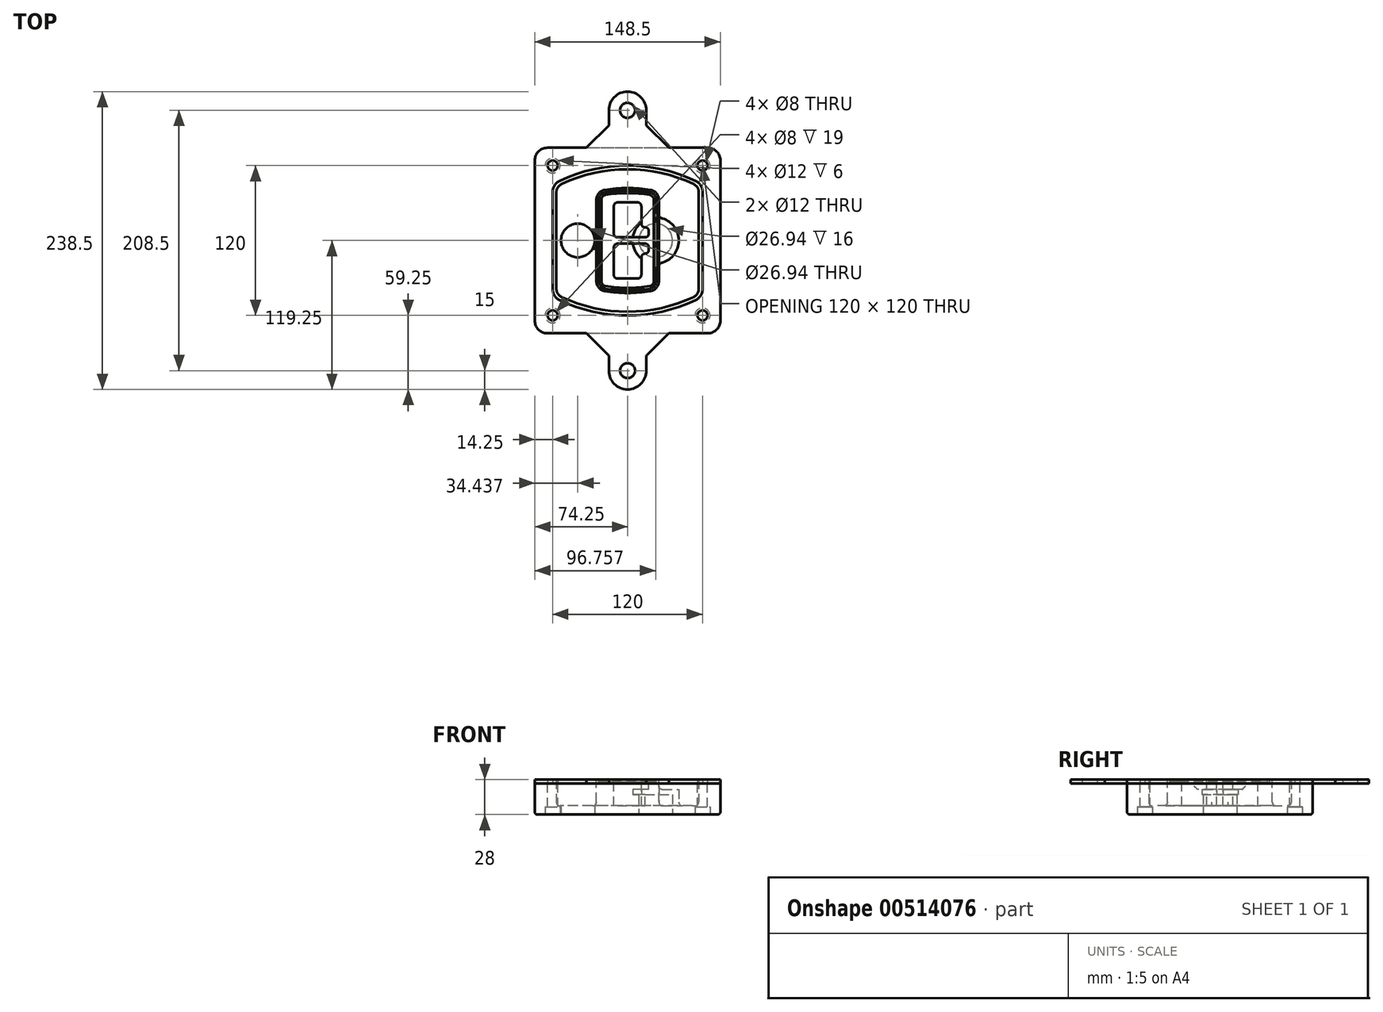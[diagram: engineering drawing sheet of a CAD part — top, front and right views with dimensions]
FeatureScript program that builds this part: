
annotation { "Feature Type Name" : "Feature", "Feature Type Description" : "" }
export const myFeature = defineFeature(function(context is Context, id is Id, definition is map)
    precondition{}
    {
        {
            var Q0;
            Q0=qCreatedBy(makeId("Top.planeOp"),FACE);
            var sketch = newSketch(context, id + "F0", { "sketchPlane" : qUnion([Q0])});
            skPoint(sketch, "E0.rect.middle", {"position": v(0, 0) * mm});
            skLineSegment(sketch, "E1.bottom", {"start": v(-64.25, -74.25) * mm, "end": v(64.25, -74.25) * mm});
            skLineSegment(sketch, "E1.top", {"start": v(-64.25, 74.25) * mm, "end": v(64.25, 74.25) * mm});
            skLineSegment(sketch, "E1.left", {"start": v(-74.25, -64.25) * mm, "end": v(-74.25, 64.25) * mm});
            skLineSegment(sketch, "E1.right", {"start": v(74.25, -64.25) * mm, "end": v(74.25, 64.25) * mm});
            skLineSegment(sketch, "E2", {"start": v(-74.25, 74.25) * mm, "end": v(74.25, -74.25) * mm, "construction": true});
            skLineSegment(sketch, "E3", {"start": v(74.25, 74.25) * mm, "end": v(-74.25, -74.25) * mm, "construction": true});
            skCircle(sketch, "E4", {"center": v(-60, 60) * mm, "radius": 4 * mm});
            skCircle(sketch, "E5", {"center": v(60, 60) * mm, "radius": 4 * mm});
            skCircle(sketch, "E6", {"center": v(60, -60) * mm, "radius": 4 * mm});
            skCircle(sketch, "E7", {"center": v(-60, -60) * mm, "radius": 4 * mm});
            skLineSegment(sketch, "E8", {"start": v(-60, 60) * mm, "end": v(60, 60) * mm, "construction": true});
            skLineSegment(sketch, "E9", {"start": v(60, 60) * mm, "end": v(60, -60) * mm, "construction": true});
            skLineSegment(sketch, "E10", {"start": v(60, -60) * mm, "end": v(-60, -60) * mm, "construction": true});
            skLineSegment(sketch, "E11", {"start": v(-60, -60) * mm, "end": v(-60, 60) * mm, "construction": true});
            skLineSegment(sketch, "E12", {"start": v(-60, 38.83) * mm, "end": v(-60, -38.83) * mm});
            skLineSegment(sketch, "E13", {"start": v(60, 38.83) * mm, "end": v(60, -38.83) * mm});
            skArc(sketch, "E14", {"start": v(54.26, 47.88) * mm, "mid": v(0, 60) * mm, "end": v(-54.26, 47.88) * mm});
            skArc(sketch, "E15", {"start": v(-54.26, -47.88) * mm, "mid": v(0, -60) * mm, "end": v(54.26, -47.88) * mm});
            skLineSegment(sketch, "E16", {"start": v(-60, 0) * mm, "end": v(60, 0) * mm, "construction": true});
            skPoint(sketch, "E17.visualSharp", {"position": v(-60, -45) * mm});
            skArc(sketch, "E17.filletArc", {"start": v(-60, -38.83) * mm, "mid": v(-58.44, -44.2) * mm, "end": v(-54.26, -47.88) * mm});
            skPoint(sketch, "E18.visualSharp", {"position": v(-60, 45) * mm});
            skArc(sketch, "E18.filletArc", {"start": v(-54.26, 47.88) * mm, "mid": v(-58.44, 44.2) * mm, "end": v(-60, 38.83) * mm});
            skPoint(sketch, "E19.visualSharp", {"position": v(60, 45) * mm});
            skArc(sketch, "E19.filletArc", {"start": v(60, 38.83) * mm, "mid": v(58.44, 44.2) * mm, "end": v(54.26, 47.88) * mm});
            skPoint(sketch, "E20.visualSharp", {"position": v(60, -45) * mm});
            skArc(sketch, "E20.filletArc", {"start": v(54.26, -47.88) * mm, "mid": v(58.44, -44.2) * mm, "end": v(60, -38.83) * mm});
            skPoint(sketch, "E21.visualSharp", {"position": v(-74.25, 74.25) * mm});
            skArc(sketch, "E21.filletArc", {"start": v(-64.25, 74.25) * mm, "mid": v(-71.32, 71.32) * mm, "end": v(-74.25, 64.25) * mm});
            skPoint(sketch, "E22.visualSharp", {"position": v(74.25, 74.25) * mm});
            skArc(sketch, "E22.filletArc", {"start": v(74.25, 64.25) * mm, "mid": v(71.32, 71.32) * mm, "end": v(64.25, 74.25) * mm});
            skPoint(sketch, "E23.visualSharp", {"position": v(74.25, -74.25) * mm});
            skArc(sketch, "E23.filletArc", {"start": v(64.25, -74.25) * mm, "mid": v(71.32, -71.32) * mm, "end": v(74.25, -64.25) * mm});
            skPoint(sketch, "E24.visualSharp", {"position": v(-74.25, -74.25) * mm});
            skArc(sketch, "E24.filletArc", {"start": v(-74.25, -64.25) * mm, "mid": v(-71.32, -71.32) * mm, "end": v(-64.25, -74.25) * mm});
            skArc(sketch, "E25.0", {"start": v(57, 38.83) * mm, "mid": v(55.9, 42.58) * mm, "end": v(52.98, 45.17) * mm});
            skLineSegment(sketch, "E25.1", {"start": v(57, 38.83) * mm, "end": v(57, -38.83) * mm});
            skArc(sketch, "E25.2", {"start": v(52.98, -45.17) * mm, "mid": v(55.9, -42.58) * mm, "end": v(57, -38.83) * mm});
            skArc(sketch, "E25.3", {"start": v(-52.98, -45.17) * mm, "mid": v(0, -57) * mm, "end": v(52.98, -45.17) * mm});
            skArc(sketch, "E25.4", {"start": v(-57, -38.83) * mm, "mid": v(-55.9, -42.58) * mm, "end": v(-52.98, -45.17) * mm});
            skArc(sketch, "E25.5", {"start": v(52.98, 45.17) * mm, "mid": v(0, 57) * mm, "end": v(-52.98, 45.17) * mm});
            skLineSegment(sketch, "E25.6", {"start": v(-57, 38.83) * mm, "end": v(-57, -38.83) * mm});
            skArc(sketch, "E25.7", {"start": v(-52.98, 45.17) * mm, "mid": v(-55.9, 42.58) * mm, "end": v(-57, 38.83) * mm});
            skArc(sketch, "E26.0", {"start": v(-55.96, 51.5) * mm, "mid": v(-61.82, 46.33) * mm, "end": v(-64, 38.83) * mm});
            skArc(sketch, "E26.1", {"start": v(55.96, 51.5) * mm, "mid": v(0, 64) * mm, "end": v(-55.96, 51.5) * mm});
            skArc(sketch, "E26.2", {"start": v(64, 38.83) * mm, "mid": v(61.82, 46.33) * mm, "end": v(55.96, 51.5) * mm});
            skLineSegment(sketch, "E26.3", {"start": v(64, 38.83) * mm, "end": v(64, -38.83) * mm});
            skArc(sketch, "E26.4", {"start": v(55.96, -51.5) * mm, "mid": v(61.82, -46.33) * mm, "end": v(64, -38.83) * mm});
            skLineSegment(sketch, "E26.5", {"start": v(-64, 38.83) * mm, "end": v(-64, -38.83) * mm});
            skArc(sketch, "E26.6", {"start": v(-55.96, -51.5) * mm, "mid": v(0, -64) * mm, "end": v(55.96, -51.5) * mm});
            skArc(sketch, "E26.7", {"start": v(-64, -38.83) * mm, "mid": v(-61.82, -46.33) * mm, "end": v(-55.96, -51.5) * mm});
            skSolve(sketch);
        }
        {
            var Q0;
            Q0=makeQuery(id+"F0.imprint","IMPRINT",FACE,{"disambiguationData":[TD([[makeQuery(id+"F0.imprint","IMPRINT",EDGE,{"derivedFrom":sQuery(id+"F0.wireOp",EDGE,"E1.bottom")}),1.0]])]});
            var Q1;
            Q1=makeQuery(id+"F0.imprint","IMPRINT",FACE,{"disambiguationData":[TD([[makeQuery(id+"F0.imprint","IMPRINT",EDGE,{"derivedFrom":sQuery(id+"F0.wireOp",EDGE,"E12")}),1.0]])]});
            var Q2;
            Q2=makeQuery(id+"F0.imprint","IMPRINT",FACE,{"disambiguationData":[TD([[makeQuery(id+"F0.imprint","IMPRINT",EDGE,{"derivedFrom":sQuery(id+"F0.wireOp",EDGE,"E25.0")}),1.0]])]});
            var Q3;
            Q3=makeQuery(id+"F0.imprint","IMPRINT",FACE,{"disambiguationData":[TD([[makeQuery(id+"F0.imprint","IMPRINT",EDGE,{"derivedFrom":sQuery(id+"F0.wireOp",EDGE,"E12")}),-1.0]])]});
            extrude(context, id + "F1", {"entities" : qUnion([Q0, Q1, Q2, Q3]), "oppositeDirection" : true, "depth" : 25 * mm});
        }
        {
            var Q0;
            Q0=makeQuery(id+"F0.imprint","IMPRINT",FACE,{"disambiguationData":[TD([[makeQuery(id+"F0.imprint","IMPRINT",EDGE,{"derivedFrom":sQuery(id+"F0.wireOp",EDGE,"E12")}),1.0]])]});
            extrude(context, id + "F2", {"entities" : qUnion([Q0]), "operationType" : NewBodyOperationType.ADD, "depth" : 3 * mm});
        }
        {
            var Q0;
            Q0=makeQuery(id+"F0.imprint","IMPRINT",FACE,{"disambiguationData":[TD([[makeQuery(id+"F0.imprint","IMPRINT",EDGE,{"derivedFrom":sQuery(id+"F0.wireOp",EDGE,"E25.0")}),1.0]])]});
            extrude(context, id + "F3", {"entities" : qUnion([Q0]), "operationType" : NewBodyOperationType.REMOVE, "oppositeDirection" : true, "depth" : 18 * mm});
        }
        {
            var Q0;
            Q0=makeQuery(id+"F2.opExtrude","CAP_FACE",FACE,{"disambiguationData":[OSD([sQuery(id+"F0.wireOp",EDGE,"E12"),sQuery(id+"F0.wireOp",EDGE,"E13"),sQuery(id+"F0.wireOp",EDGE,"E14"),sQuery(id+"F0.wireOp",EDGE,"E15"),sQuery(id+"F0.wireOp",EDGE,"E17.filletArc"),sQuery(id+"F0.wireOp",EDGE,"E18.filletArc"),sQuery(id+"F0.wireOp",EDGE,"E19.filletArc"),sQuery(id+"F0.wireOp",EDGE,"E20.filletArc"),sQuery(id+"F0.wireOp",EDGE,"E25.0"),sQuery(id+"F0.wireOp",EDGE,"E25.1"),sQuery(id+"F0.wireOp",EDGE,"E25.2"),sQuery(id+"F0.wireOp",EDGE,"E25.3"),sQuery(id+"F0.wireOp",EDGE,"E25.4"),sQuery(id+"F0.wireOp",EDGE,"E25.5"),sQuery(id+"F0.wireOp",EDGE,"E25.6"),sQuery(id+"F0.wireOp",EDGE,"E25.7")])],"isStart":false});
            var sketch = newSketch(context, id + "F4", { "sketchPlane" : qUnion([Q0])});
            skArc(sketch, "E27.0", {"start": v(-18.34, -40.45) * mm, "mid": v(0, -42) * mm, "end": v(18.34, -40.45) * mm});
            skArc(sketch, "E28.0", {"start": v(18.34, 40.45) * mm, "mid": v(0, 42) * mm, "end": v(-18.34, 40.45) * mm});
            skLineSegment(sketch, "E29", {"start": v(-25, 32.57) * mm, "end": v(-25, -32.57) * mm});
            skLineSegment(sketch, "E30", {"start": v(25, 32.57) * mm, "end": v(25, -32.57) * mm});
            skLineSegment(sketch, "E31", {"start": v(-25, 39.1) * mm, "end": v(25, 39.1) * mm, "construction": true});
            skLineSegment(sketch, "E32", {"start": v(-25, -39.1) * mm, "end": v(25, -39.1) * mm, "construction": true});
            skPoint(sketch, "E33.visualSharp", {"position": v(-25, 39.1) * mm});
            skArc(sketch, "E33.filletArc", {"start": v(-18.34, 40.45) * mm, "mid": v(-23.11, 37.73) * mm, "end": v(-25, 32.57) * mm});
            skPoint(sketch, "E34.visualSharp", {"position": v(25, 39.1) * mm});
            skArc(sketch, "E34.filletArc", {"start": v(25, 32.57) * mm, "mid": v(23.11, 37.73) * mm, "end": v(18.34, 40.45) * mm});
            skPoint(sketch, "E35.visualSharp", {"position": v(25, -39.1) * mm});
            skArc(sketch, "E35.filletArc", {"start": v(18.34, -40.45) * mm, "mid": v(23.11, -37.73) * mm, "end": v(25, -32.57) * mm});
            skPoint(sketch, "E36.visualSharp", {"position": v(-25, -39.1) * mm});
            skArc(sketch, "E36.filletArc", {"start": v(-25, -32.57) * mm, "mid": v(-23.11, -37.73) * mm, "end": v(-18.34, -40.45) * mm});
            skArc(sketch, "E37.0", {"start": v(52.98, 45.17) * mm, "mid": v(0, 57) * mm, "end": v(-52.98, 45.17) * mm});
            skArc(sketch, "E37.1", {"start": v(-52.98, 45.17) * mm, "mid": v(-55.9, 42.58) * mm, "end": v(-57, 38.83) * mm});
            skLineSegment(sketch, "E37.2", {"start": v(-57, 38.83) * mm, "end": v(-57, -38.83) * mm});
            skArc(sketch, "E37.3", {"start": v(-57, -38.83) * mm, "mid": v(-55.9, -42.58) * mm, "end": v(-52.98, -45.17) * mm});
            skArc(sketch, "E37.4", {"start": v(-52.98, -45.17) * mm, "mid": v(0, -57) * mm, "end": v(52.98, -45.17) * mm});
            skArc(sketch, "E37.5", {"start": v(52.98, -45.17) * mm, "mid": v(55.9, -42.58) * mm, "end": v(57, -38.83) * mm});
            skLineSegment(sketch, "E37.6", {"start": v(57, 38.83) * mm, "end": v(57, -38.83) * mm});
            skArc(sketch, "E37.7", {"start": v(57, 38.83) * mm, "mid": v(55.9, 42.58) * mm, "end": v(52.98, 45.17) * mm});
            skLineSegment(sketch, "E38.0", {"start": v(23, 32.57) * mm, "end": v(23, -32.57) * mm});
            skArc(sketch, "E38.1", {"start": v(18, -38.48) * mm, "mid": v(21.58, -36.44) * mm, "end": v(23, -32.57) * mm});
            skArc(sketch, "E38.2", {"start": v(-18, -38.48) * mm, "mid": v(0, -40) * mm, "end": v(18, -38.48) * mm});
            skArc(sketch, "E38.3", {"start": v(-23, -32.57) * mm, "mid": v(-21.58, -36.44) * mm, "end": v(-18, -38.48) * mm});
            skLineSegment(sketch, "E38.4", {"start": v(-23, 32.57) * mm, "end": v(-23, -32.57) * mm});
            skArc(sketch, "E38.5", {"start": v(23, 32.57) * mm, "mid": v(21.58, 36.44) * mm, "end": v(18, 38.48) * mm});
            skArc(sketch, "E38.6", {"start": v(-18, 38.48) * mm, "mid": v(-21.58, 36.44) * mm, "end": v(-23, 32.57) * mm});
            skArc(sketch, "E38.7", {"start": v(18, 38.48) * mm, "mid": v(0, 40) * mm, "end": v(-18, 38.48) * mm});
            skArc(sketch, "E39.0", {"start": v(21, 32.57) * mm, "mid": v(20.06, 35.15) * mm, "end": v(17.67, 36.5) * mm});
            skLineSegment(sketch, "E39.1", {"start": v(21, 32.57) * mm, "end": v(21, -32.57) * mm});
            skArc(sketch, "E39.2", {"start": v(17.67, -36.5) * mm, "mid": v(20.06, -35.15) * mm, "end": v(21, -32.57) * mm});
            skArc(sketch, "E39.3", {"start": v(-17.67, -36.5) * mm, "mid": v(0, -38) * mm, "end": v(17.67, -36.5) * mm});
            skArc(sketch, "E39.4", {"start": v(-21, -32.57) * mm, "mid": v(-20.06, -35.15) * mm, "end": v(-17.67, -36.5) * mm});
            skArc(sketch, "E39.5", {"start": v(17.67, 36.5) * mm, "mid": v(0, 38) * mm, "end": v(-17.67, 36.5) * mm});
            skLineSegment(sketch, "E39.6", {"start": v(-21, 32.57) * mm, "end": v(-21, -32.57) * mm});
            skArc(sketch, "E39.7", {"start": v(-17.67, 36.5) * mm, "mid": v(-20.06, 35.15) * mm, "end": v(-21, 32.57) * mm});
            skLineSegment(sketch, "E40", {"start": v(-25, 0) * mm, "end": v(25, 0) * mm, "construction": true});
            skLineSegment(sketch, "E41", {"start": v(-11, 5.5) * mm, "end": v(-11, 27.5) * mm});
            skLineSegment(sketch, "E42", {"start": v(-8, 30.5) * mm, "end": v(8, 30.5) * mm});
            skLineSegment(sketch, "E43", {"start": v(11, 27.5) * mm, "end": v(11, 13.5) * mm});
            skLineSegment(sketch, "E44", {"start": v(14, 10.5) * mm, "end": v(14, 10.5) * mm});
            skLineSegment(sketch, "E45", {"start": v(17, 7.5) * mm, "end": v(17, 5.5) * mm});
            skLineSegment(sketch, "E46", {"start": v(14, 2.5) * mm, "end": v(-8, 2.5) * mm});
            skPoint(sketch, "E47.visualSharp", {"position": v(-11, 30.5) * mm});
            skArc(sketch, "E47.filletArc", {"start": v(-8, 30.5) * mm, "mid": v(-10.12, 29.62) * mm, "end": v(-11, 27.5) * mm});
            skPoint(sketch, "E48.visualSharp", {"position": v(11, 30.5) * mm});
            skArc(sketch, "E48.filletArc", {"start": v(11, 27.5) * mm, "mid": v(10.12, 29.62) * mm, "end": v(8, 30.5) * mm});
            skPoint(sketch, "E49.visualSharp", {"position": v(11, 10.5) * mm});
            skArc(sketch, "E49.filletArc", {"start": v(11, 13.5) * mm, "mid": v(11.88, 11.38) * mm, "end": v(14, 10.5) * mm});
            skPoint(sketch, "E50.visualSharp", {"position": v(17, 10.5) * mm});
            skArc(sketch, "E50.filletArc", {"start": v(17, 7.5) * mm, "mid": v(16.12, 9.62) * mm, "end": v(14, 10.5) * mm});
            skPoint(sketch, "E51.visualSharp", {"position": v(17, 2.5) * mm});
            skArc(sketch, "E51.filletArc", {"start": v(14, 2.5) * mm, "mid": v(16.12, 3.38) * mm, "end": v(17, 5.5) * mm});
            skPoint(sketch, "E52.visualSharp", {"position": v(-11, 2.5) * mm});
            skArc(sketch, "E52.filletArc", {"start": v(-11, 5.5) * mm, "mid": v(-10.12, 3.38) * mm, "end": v(-8, 2.5) * mm});
            skLineSegment(sketch, "E53.0.MirrorCS", {"start": v(14, -2.5) * mm, "end": v(-8, -2.5) * mm});
            skArc(sketch, "E54.0.MirrorCS", {"start": v(-11, -5.5) * mm, "mid": v(-10.12, -3.38) * mm, "end": v(-8, -2.5) * mm});
            skLineSegment(sketch, "E55.0.MirrorCS", {"start": v(-11, -5.5) * mm, "end": v(-11, -27.5) * mm});
            skArc(sketch, "E56.0.MirrorCS", {"start": v(-8, -30.5) * mm, "mid": v(-10.12, -29.62) * mm, "end": v(-11, -27.5) * mm});
            skLineSegment(sketch, "E57.0.MirrorCS", {"start": v(-8, -30.5) * mm, "end": v(8, -30.5) * mm});
            skArc(sketch, "E58.0.MirrorCS", {"start": v(11, -27.5) * mm, "mid": v(10.12, -29.62) * mm, "end": v(8, -30.5) * mm});
            skLineSegment(sketch, "E59.0.MirrorCS", {"start": v(11, -27.5) * mm, "end": v(11, -13.5) * mm});
            skArc(sketch, "E60.0.MirrorCS", {"start": v(11, -13.5) * mm, "mid": v(11.88, -11.38) * mm, "end": v(14, -10.5) * mm});
            skArc(sketch, "E61.0.MirrorCS", {"start": v(17, -7.5) * mm, "mid": v(16.12, -9.62) * mm, "end": v(14, -10.5) * mm});
            skLineSegment(sketch, "E62.0.MirrorCS", {"start": v(17, -7.5) * mm, "end": v(17, -5.5) * mm});
            skArc(sketch, "E63.0.MirrorCS", {"start": v(14, -2.5) * mm, "mid": v(16.12, -3.38) * mm, "end": v(17, -5.5) * mm});
            skSolve(sketch);
        }
        {
            var Q0;
            Q0=makeQuery(id+"F4.imprint","IMPRINT",FACE,{"disambiguationData":[TD([[makeQuery(id+"F4.imprint","IMPRINT",EDGE,{"derivedFrom":sQuery(id+"F4.wireOp",EDGE,"E27.0")}),1.0]])]});
            var Q1;
            Q1=makeQuery(id+"F4.imprint","IMPRINT",FACE,{"disambiguationData":[TD([[makeQuery(id+"F4.imprint","IMPRINT",EDGE,{"derivedFrom":sQuery(id+"F4.wireOp",EDGE,"E38.0")}),-1.0]])]});
            var Q2;
            Q2=makeQuery(id+"F4.imprint","IMPRINT",FACE,{"disambiguationData":[TD([[makeQuery(id+"F4.imprint","IMPRINT",EDGE,{"derivedFrom":sQuery(id+"F4.wireOp",EDGE,"E39.0")}),1.0]])]});
            extrude(context, id + "F5", {"entities" : qUnion([Q0, Q1, Q2]), "operationType" : NewBodyOperationType.ADD, "endBound" : BoundingType.UP_TO_NEXT, "oppositeDirection" : true, "depth" : 25 * mm});
        }
        {
            var Q0;
            Q0=makeQuery(id+"F4.imprint","IMPRINT",FACE,{"disambiguationData":[TD([[makeQuery(id+"F4.imprint","IMPRINT",EDGE,{"derivedFrom":sQuery(id+"F4.wireOp",EDGE,"E38.0")}),-1.0]])]});
            extrude(context, id + "F6", {"entities" : qUnion([Q0]), "operationType" : NewBodyOperationType.REMOVE, "oppositeDirection" : true, "depth" : 2 * mm});
        }
        {
            var Q0;
            Q0=makeQuery(id+"F1.opExtrude","CAP_FACE",FACE,{"disambiguationData":[OSD([sQuery(id+"F0.wireOp",EDGE,"E1.bottom"),sQuery(id+"F0.wireOp",EDGE,"E1.top"),sQuery(id+"F0.wireOp",EDGE,"E1.left"),sQuery(id+"F0.wireOp",EDGE,"E1.right"),sQuery(id+"F0.wireOp",EDGE,"E4"),sQuery(id+"F0.wireOp",EDGE,"E5"),sQuery(id+"F0.wireOp",EDGE,"E6"),sQuery(id+"F0.wireOp",EDGE,"E7"),sQuery(id+"F0.wireOp",EDGE,"E21.filletArc"),sQuery(id+"F0.wireOp",EDGE,"E22.filletArc"),sQuery(id+"F0.wireOp",EDGE,"E23.filletArc"),sQuery(id+"F0.wireOp",EDGE,"E24.filletArc")])],"isStart":false});
            var sketch = newSketch(context, id + "F7", { "sketchPlane" : qUnion([Q0])});
            skCircle(sketch, "E64", {"center": v(22.5, 0) * mm, "radius": 13.47 * mm});
            skCircle(sketch, "E65", {"center": v(-39.81, 0) * mm, "radius": 13.47 * mm});
            skLineSegment(sketch, "E66", {"start": v(74.25, 0) * mm, "end": v(-74.25, 0) * mm});
            skCircle(sketch, "E67", {"center": v(22.5, 0) * mm, "radius": 18.47 * mm});
            skCircle(sketch, "E68", {"center": v(60, -60) * mm, "radius": 6 * mm});
            skCircle(sketch, "E69", {"center": v(-60, -60) * mm, "radius": 6 * mm});
            skCircle(sketch, "E70", {"center": v(-60, 60) * mm, "radius": 6 * mm});
            skCircle(sketch, "E71", {"center": v(60, 60) * mm, "radius": 6 * mm});
            skSolve(sketch);
        }
        {
            var Q0;
            {var subQ1=sQuery(id+"F7.wireOp",EDGE,"E66");var subQ4=sQuery(id+"F7.wireOp",EDGE,"E64");var subQ6=makeQuery(id+"F7.imprint","INTERSECT",VERTEX,{"disambiguationData":[OD(0.0)],"derivedFrom":[subQ4,subQ1]});Q0=makeQuery(id+"F7.imprint","IMPRINT",FACE,{"disambiguationData":[TD([[makeQuery(id+"F7.imprint","IMPRINT",EDGE,{"disambiguationData":[TD([[subQ6,-1.0]])],"derivedFrom":subQ4}),-1.0]])]});}
            var Q1;
            {var subQ0=sQuery(id+"F7.wireOp",EDGE,"E66");var subQ1=sQuery(id+"F7.wireOp",EDGE,"E64");var subQ3=makeQuery(id+"F7.imprint","INTERSECT",VERTEX,{"disambiguationData":[OD(0.0)],"derivedFrom":[subQ1,subQ0]});Q1=makeQuery(id+"F7.imprint","IMPRINT",FACE,{"disambiguationData":[TD([[makeQuery(id+"F7.imprint","IMPRINT",EDGE,{"disambiguationData":[TD([[subQ3,-1.0]])],"derivedFrom":subQ1}),1.0]])]});}
            var Q2;
            {var subQ0=sQuery(id+"F7.wireOp",EDGE,"E66");var subQ1=sQuery(id+"F7.wireOp",EDGE,"E64");var subQ3=makeQuery(id+"F7.imprint","INTERSECT",VERTEX,{"disambiguationData":[OD(0.0)],"derivedFrom":[subQ1,subQ0]});Q2=makeQuery(id+"F7.imprint","IMPRINT",FACE,{"disambiguationData":[TD([[makeQuery(id+"F7.imprint","IMPRINT",EDGE,{"disambiguationData":[TD([[subQ3,1.0]])],"derivedFrom":subQ1}),1.0]])]});}
            var Q3;
            {var subQ1=sQuery(id+"F7.wireOp",EDGE,"E66");var subQ4=sQuery(id+"F7.wireOp",EDGE,"E64");var subQ6=makeQuery(id+"F7.imprint","INTERSECT",VERTEX,{"disambiguationData":[OD(0.0)],"derivedFrom":[subQ4,subQ1]});Q3=makeQuery(id+"F7.imprint","IMPRINT",FACE,{"disambiguationData":[TD([[makeQuery(id+"F7.imprint","IMPRINT",EDGE,{"disambiguationData":[TD([[subQ6,1.0]])],"derivedFrom":subQ4}),-1.0]])]});}
            extrude(context, id + "F8", {"entities" : qUnion([Q0, Q1, Q2, Q3]), "operationType" : NewBodyOperationType.ADD, "oppositeDirection" : true, "depth" : 20 * mm});
        }
        {
            var Q0;
            {var subQ0=sQuery(id+"F7.wireOp",EDGE,"E66");var subQ1=sQuery(id+"F7.wireOp",EDGE,"E64");var subQ3=makeQuery(id+"F7.imprint","INTERSECT",VERTEX,{"disambiguationData":[OD(0.0)],"derivedFrom":[subQ1,subQ0]});Q0=makeQuery(id+"F7.imprint","IMPRINT",FACE,{"disambiguationData":[TD([[makeQuery(id+"F7.imprint","IMPRINT",EDGE,{"disambiguationData":[TD([[subQ3,-1.0]])],"derivedFrom":subQ1}),1.0]])]});}
            var Q1;
            {var subQ0=sQuery(id+"F7.wireOp",EDGE,"E66");var subQ1=sQuery(id+"F7.wireOp",EDGE,"E64");var subQ3=makeQuery(id+"F7.imprint","INTERSECT",VERTEX,{"disambiguationData":[OD(0.0)],"derivedFrom":[subQ1,subQ0]});Q1=makeQuery(id+"F7.imprint","IMPRINT",FACE,{"disambiguationData":[TD([[makeQuery(id+"F7.imprint","IMPRINT",EDGE,{"disambiguationData":[TD([[subQ3,1.0]])],"derivedFrom":subQ1}),1.0]])]});}
            extrude(context, id + "F9", {"entities" : qUnion([Q0, Q1]), "operationType" : NewBodyOperationType.REMOVE, "oppositeDirection" : true, "depth" : 16 * mm});
        }
        {
            var Q0;
            {var subQ0=sQuery(id+"F7.wireOp",EDGE,"E66");var subQ1=sQuery(id+"F7.wireOp",EDGE,"E65");var subQ3=makeQuery(id+"F7.imprint","INTERSECT",VERTEX,{"disambiguationData":[OD(0.0)],"derivedFrom":[subQ1,subQ0]});Q0=makeQuery(id+"F7.imprint","IMPRINT",FACE,{"disambiguationData":[TD([[makeQuery(id+"F7.imprint","IMPRINT",EDGE,{"disambiguationData":[TD([[subQ3,-1.0]])],"derivedFrom":subQ1}),1.0]])]});}
            var Q1;
            {var subQ0=sQuery(id+"F7.wireOp",EDGE,"E66");var subQ1=sQuery(id+"F7.wireOp",EDGE,"E65");var subQ3=makeQuery(id+"F7.imprint","INTERSECT",VERTEX,{"disambiguationData":[OD(0.0)],"derivedFrom":[subQ1,subQ0]});Q1=makeQuery(id+"F7.imprint","IMPRINT",FACE,{"disambiguationData":[TD([[makeQuery(id+"F7.imprint","IMPRINT",EDGE,{"disambiguationData":[TD([[subQ3,1.0]])],"derivedFrom":subQ1}),1.0]])]});}
            extrude(context, id + "F10", {"entities" : qUnion([Q0, Q1]), "operationType" : NewBodyOperationType.REMOVE, "oppositeDirection" : true, "depth" : 25 * mm});
        }
        {
            var Q0;
            Q0=makeQuery(id+"F7.imprint","IMPRINT",FACE,{"disambiguationData":[TD([[makeQuery(id+"F7.imprint","IMPRINT",EDGE,{"derivedFrom":sQuery(id+"F7.wireOp",EDGE,"E68")}),1.0]])]});
            var Q1;
            Q1=makeQuery(id+"F7.imprint","IMPRINT",FACE,{"disambiguationData":[TD([[makeQuery(id+"F7.imprint","IMPRINT",EDGE,{"derivedFrom":makeQuery(id+"F1.opExtrude","CAP_EDGE",EDGE,{"disambiguationData":[OSD([sQuery(id+"F0.wireOp",EDGE,"E5")])],"isStart":false})}),-1.0]])]});
            var Q2;
            Q2=makeQuery(id+"F7.imprint","IMPRINT",FACE,{"disambiguationData":[TD([[makeQuery(id+"F7.imprint","IMPRINT",EDGE,{"derivedFrom":sQuery(id+"F7.wireOp",EDGE,"E69")}),1.0]])]});
            var Q3;
            Q3=makeQuery(id+"F7.imprint","IMPRINT",FACE,{"disambiguationData":[TD([[makeQuery(id+"F7.imprint","IMPRINT",EDGE,{"derivedFrom":makeQuery(id+"F1.opExtrude","CAP_EDGE",EDGE,{"disambiguationData":[OSD([sQuery(id+"F0.wireOp",EDGE,"E4")])],"isStart":false})}),-1.0]])]});
            var Q4;
            Q4=makeQuery(id+"F7.imprint","IMPRINT",FACE,{"disambiguationData":[TD([[makeQuery(id+"F7.imprint","IMPRINT",EDGE,{"derivedFrom":sQuery(id+"F7.wireOp",EDGE,"E70")}),1.0]])]});
            var Q5;
            Q5=makeQuery(id+"F7.imprint","IMPRINT",FACE,{"disambiguationData":[TD([[makeQuery(id+"F7.imprint","IMPRINT",EDGE,{"derivedFrom":makeQuery(id+"F1.opExtrude","CAP_EDGE",EDGE,{"disambiguationData":[OSD([sQuery(id+"F0.wireOp",EDGE,"E7")])],"isStart":false})}),-1.0]])]});
            var Q6;
            Q6=makeQuery(id+"F7.imprint","IMPRINT",FACE,{"disambiguationData":[TD([[makeQuery(id+"F7.imprint","IMPRINT",EDGE,{"derivedFrom":sQuery(id+"F7.wireOp",EDGE,"E71")}),1.0]])]});
            var Q7;
            Q7=makeQuery(id+"F7.imprint","IMPRINT",FACE,{"disambiguationData":[TD([[makeQuery(id+"F7.imprint","IMPRINT",EDGE,{"derivedFrom":makeQuery(id+"F1.opExtrude","CAP_EDGE",EDGE,{"disambiguationData":[OSD([sQuery(id+"F0.wireOp",EDGE,"E6")])],"isStart":false})}),-1.0]])]});
            extrude(context, id + "F11", {"entities" : qUnion([Q0, Q1, Q2, Q3, Q4, Q5, Q6, Q7]), "operationType" : NewBodyOperationType.REMOVE, "oppositeDirection" : true, "depth" : 6 * mm});
        }
        {
            var Q0;
            Q0=makeQuery(id+"F9.boolean.opBoolean","COPY",FACE,{"derivedFrom":makeQuery(id+"F9.opExtrude","CAP_FACE",FACE,{"disambiguationData":[OSD([sQuery(id+"F7.wireOp",EDGE,"E64")])],"isStart":false})});
            var sketch = newSketch(context, id + "F12", { "sketchPlane" : qUnion([Q0])});
            skArc(sketch, "E72.0", {"start": v(11, 14.45) * mm, "mid": v(6.45, 9.13) * mm, "end": v(4.2, 2.5) * mm});
            skArc(sketch, "E72.1", {"start": v(4.2, -2.5) * mm, "mid": v(6.45, -9.13) * mm, "end": v(11, -14.45) * mm});
            skLineSegment(sketch, "E73", {"start": v(4.2, -2.5) * mm, "end": v(14, -2.5) * mm});
            skLineSegment(sketch, "E74.0", {"start": v(14, 2.5) * mm, "end": v(4.2, 2.5) * mm});
            skArc(sketch, "E74.1", {"start": v(14, 2.5) * mm, "mid": v(16.12, 3.38) * mm, "end": v(17, 5.5) * mm});
            skLineSegment(sketch, "E74.2", {"start": v(17, 7.5) * mm, "end": v(17, 5.5) * mm});
            skArc(sketch, "E74.3", {"start": v(17, 7.5) * mm, "mid": v(16.12, 9.62) * mm, "end": v(14, 10.5) * mm});
            skArc(sketch, "E74.4", {"start": v(11, 13.5) * mm, "mid": v(11.88, 11.38) * mm, "end": v(14, 10.5) * mm});
            skLineSegment(sketch, "E74.5", {"start": v(11, 14.45) * mm, "end": v(11, 13.5) * mm});
            skLineSegment(sketch, "E74.7", {"start": v(14, -2.5) * mm, "end": v(4.2, -2.5) * mm});
            skArc(sketch, "E74.8", {"start": v(14, -2.5) * mm, "mid": v(16.12, -3.38) * mm, "end": v(17, -5.5) * mm});
            skLineSegment(sketch, "E74.9", {"start": v(17, -7.5) * mm, "end": v(17, -5.5) * mm});
            skArc(sketch, "E74.10", {"start": v(17, -7.5) * mm, "mid": v(16.12, -9.62) * mm, "end": v(14, -10.5) * mm});
            skArc(sketch, "E74.11", {"start": v(11, -13.5) * mm, "mid": v(11.88, -11.38) * mm, "end": v(14, -10.5) * mm});
            skLineSegment(sketch, "E74.12", {"start": v(11, -14.45) * mm, "end": v(11, -13.5) * mm});
            skPoint(sketch, "E75.orphan", {"position": v(11, -27.5) * mm});
            skPoint(sketch, "E76.orphan", {"position": v(-8, -2.5) * mm});
            skPoint(sketch, "E77.orphan", {"position": v(-8, 2.5) * mm});
            skPoint(sketch, "E78.orphan", {"position": v(11, 27.5) * mm});
            skSolve(sketch);
        }
        {
            var Q0;
            {var subQ7=sQuery(id+"F12.wireOp",EDGE,"E72.0");var subQ14=sQuery(id+"F12.wireOp",EDGE,"E72.1");var subQ16=sQuery(id+"F12.wireOp",EDGE,"E74.1");var subQ18=sQuery(id+"F12.wireOp",EDGE,"E74.8");Q0=qUnion([makeQuery(id+"F12.imprint","IMPRINT",FACE,{"disambiguationData":[TD([[makeQuery(id+"F12.imprint","IMPRINT",EDGE,{"derivedFrom":subQ7}),1.0]])]}),makeQuery(id+"F12.imprint","IMPRINT",FACE,{"disambiguationData":[TD([[makeQuery(id+"F12.imprint","IMPRINT",EDGE,{"derivedFrom":subQ14}),1.0]])]}),makeQuery(id+"F12.imprint","IMPRINT",FACE,{"disambiguationData":[TD([[makeQuery(id+"F12.imprint","IMPRINT",EDGE,{"derivedFrom":subQ16}),1.0]])]}),makeQuery(id+"F12.imprint","IMPRINT",FACE,{"disambiguationData":[TD([[makeQuery(id+"F12.imprint","IMPRINT",EDGE,{"derivedFrom":subQ18}),-1.0]])]})]);}
            var Q1;
            Q1=makeQuery(id+"F5.boolean.opBoolean","SPLIT",FACE,{"disambiguationData":[TD([makeQuery(id+"F5.opExtrude","SWEPT_FACE",FACE,{"disambiguationData":[OSD([sQuery(id+"F4.wireOp",EDGE,"E41")])]})])],"derivedFrom":makeQuery(id+"F3.boolean.opBoolean","COPY",FACE,{"derivedFrom":makeQuery(id+"F3.opExtrude","CAP_FACE",FACE,{"disambiguationData":[OSD([sQuery(id+"F0.wireOp",EDGE,"E25.0"),sQuery(id+"F0.wireOp",EDGE,"E25.1"),sQuery(id+"F0.wireOp",EDGE,"E25.2"),sQuery(id+"F0.wireOp",EDGE,"E25.3"),sQuery(id+"F0.wireOp",EDGE,"E25.4"),sQuery(id+"F0.wireOp",EDGE,"E25.5"),sQuery(id+"F0.wireOp",EDGE,"E25.6"),sQuery(id+"F0.wireOp",EDGE,"E25.7")])],"isStart":false})})});
            extrude(context, id + "F13", {"entities" : qUnion([Q0]), "operationType" : NewBodyOperationType.REMOVE, "endBound" : BoundingType.UP_TO_SURFACE, "endBoundEntityFace" : qUnion([Q1]), "depth" : 25 * mm});
        }
        {
            var Q0;
            Q0=makeQuery(id+"F3.boolean.opBoolean","COPY",EDGE,{"derivedFrom":makeQuery(id+"F3.opExtrude","CAP_EDGE",EDGE,{"disambiguationData":[OSD([sQuery(id+"F0.wireOp",EDGE,"E25.6")])],"isStart":false})});
            var Q1;
            Q1=makeQuery(id+"F8.boolean.opBoolean","INTERSECT",EDGE,{"derivedFrom":[makeQuery(id+"F5.opExtrude","SWEPT_FACE",FACE,{"disambiguationData":[OSD([sQuery(id+"F4.wireOp",EDGE,"E30")])]}),makeQuery(id+"F8.opExtrude","CAP_FACE",FACE,{"disambiguationData":[OSD([sQuery(id+"F7.wireOp",EDGE,"E67")])],"isStart":false})]});
            var Q2;
            Q2=makeQuery(id+"F8.boolean.opBoolean","INTERSECT",EDGE,{"disambiguationData":[OD(1.0)],"derivedFrom":[makeQuery(id+"F5.opExtrude","SWEPT_FACE",FACE,{"disambiguationData":[OSD([sQuery(id+"F4.wireOp",EDGE,"E30")])]}),makeQuery(id+"F8.opExtrude","SWEPT_FACE",FACE,{"disambiguationData":[OSD([sQuery(id+"F7.wireOp",EDGE,"E67")])]})]});
            var Q3;
            {var subQ0=sQuery(id+"F4.wireOp",EDGE,"E30");Q3=makeQuery(id+"F8.boolean.opBoolean","SPLIT",EDGE,{"disambiguationData":[TD([makeQuery(id+"F5.opExtrude","SWEPT_FACE",FACE,{"disambiguationData":[OSD([sQuery(id+"F4.wireOp",EDGE,"E35.filletArc")])]})])],"derivedFrom":makeQuery(id+"F5.opExtrude","CAP_EDGE",EDGE,{"disambiguationData":[OSD([subQ0])],"isStart":false})});}
            var Q4;
            {var subQ0=sQuery(id+"F0.wireOp",EDGE,"E25.7");var subQ1=sQuery(id+"F0.wireOp",EDGE,"E25.1");var subQ2=sQuery(id+"F0.wireOp",EDGE,"E25.6");var subQ3=sQuery(id+"F0.wireOp",EDGE,"E25.5");var subQ4=sQuery(id+"F0.wireOp",EDGE,"E25.4");var subQ5=sQuery(id+"F0.wireOp",EDGE,"E25.0");var subQ6=sQuery(id+"F0.wireOp",EDGE,"E25.2");var subQ7=sQuery(id+"F0.wireOp",EDGE,"E25.3");Q4=makeQuery(id+"F8.boolean.opBoolean","INTERSECT",EDGE,{"derivedFrom":[makeQuery(id+"F5.boolean.opBoolean","SPLIT",FACE,{"disambiguationData":[TD([makeQuery(id+"F2.opExtrude","SWEPT_FACE",FACE,{"disambiguationData":[OSD([subQ5])]})])],"derivedFrom":makeQuery(id+"F3.boolean.opBoolean","COPY",FACE,{"derivedFrom":makeQuery(id+"F3.opExtrude","CAP_FACE",FACE,{"disambiguationData":[OSD([subQ5,subQ1,subQ6,subQ7,subQ4,subQ3,subQ2,subQ0])],"isStart":false})})}),makeQuery(id+"F8.opExtrude","SWEPT_FACE",FACE,{"disambiguationData":[OSD([sQuery(id+"F7.wireOp",EDGE,"E67")])]})]});}
            var Q5;
            Q5=makeQuery(id+"F8.boolean.opBoolean","INTERSECT",EDGE,{"disambiguationData":[OD(0.0)],"derivedFrom":[makeQuery(id+"F5.opExtrude","SWEPT_FACE",FACE,{"disambiguationData":[OSD([sQuery(id+"F4.wireOp",EDGE,"E30")])]}),makeQuery(id+"F8.opExtrude","SWEPT_FACE",FACE,{"disambiguationData":[OSD([sQuery(id+"F7.wireOp",EDGE,"E67")])]})]});
            fillet(context, id + "F14", {"entities" : qUnion([Q0, Q1, Q2, Q3, Q4, Q5]), "radius" : 3 * mm, "tangentPropagation" : true, "allowEdgeOverflow" : false});
        }
        {
            var Q0;
            Q0=makeQuery(id+"F1.opExtrude","CAP_EDGE",EDGE,{"disambiguationData":[OSD([sQuery(id+"F0.wireOp",EDGE,"E1.bottom")])],"isStart":false});
            fillet(context, id + "F15", {"entities" : qUnion([Q0]), "radius" : 2 * mm, "tangentPropagation" : true, "allowEdgeOverflow" : false});
        }
        {
            var Q0;
            {var subQ0=sQuery(id+"F0.wireOp",EDGE,"E21.filletArc");var subQ1=sQuery(id+"F0.wireOp",EDGE,"E7");var subQ2=sQuery(id+"F0.wireOp",EDGE,"E6");var subQ3=sQuery(id+"F0.wireOp",EDGE,"E5");var subQ4=sQuery(id+"F0.wireOp",EDGE,"E4");var subQ5=sQuery(id+"F0.wireOp",EDGE,"E22.filletArc");var subQ6=sQuery(id+"F0.wireOp",EDGE,"E1.bottom");var subQ7=sQuery(id+"F0.wireOp",EDGE,"E1.right");var subQ8=sQuery(id+"F0.wireOp",EDGE,"E1.top");var subQ9=sQuery(id+"F0.wireOp",EDGE,"E1.left");var subQ10=sQuery(id+"F0.wireOp",EDGE,"E23.filletArc");var subQ11=sQuery(id+"F0.wireOp",EDGE,"E24.filletArc");Q0=makeQuery(id+"F2.boolean.opBoolean","SPLIT",FACE,{"disambiguationData":[TD([makeQuery(id+"F1.opExtrude","SWEPT_FACE",FACE,{"disambiguationData":[OSD([subQ6])]})])],"derivedFrom":makeQuery(id+"F1.opExtrude","CAP_FACE",FACE,{"disambiguationData":[OSD([subQ6,subQ8,subQ9,subQ7,subQ4,subQ3,subQ2,subQ1,subQ0,subQ5,subQ10,subQ11])],"isStart":true})});}
            var sketch = newSketch(context, id + "F16", { "sketchPlane" : qUnion([Q0])});
            skLineSegment(sketch, "E79", {"start": v(-15, 92.25) * mm, "end": v(-15, 104.25) * mm});
            skCircle(sketch, "E80", {"center": v(0, 104.25) * mm, "radius": 6 * mm});
            skLineSegment(sketch, "E81", {"start": v(0, 104.25) * mm, "end": v(0, 74.25) * mm, "construction": true});
            skPoint(sketch, "E82", {"position": v(0, 74.25) * mm});
            skArc(sketch, "E83", {"start": v(-15, 104.25) * mm, "mid": v(0, 119.25) * mm, "end": v(15, 104.25) * mm});
            skLineSegment(sketch, "E84", {"start": v(15, 104.25) * mm, "end": v(15, 92.25) * mm});
            skLineSegment(sketch, "E85.0", {"start": v(-64.25, 74.25) * mm, "end": v(64.25, 74.25) * mm});
            skArc(sketch, "E85.1", {"start": v(-64.25, 74.25) * mm, "mid": v(-71.32, 71.32) * mm, "end": v(-74.25, 64.25) * mm});
            skArc(sketch, "E85.2", {"start": v(74.25, 64.25) * mm, "mid": v(71.32, 71.32) * mm, "end": v(64.25, 74.25) * mm});
            skLineSegment(sketch, "E85.3", {"start": v(74.25, -64.25) * mm, "end": v(74.25, 64.25) * mm});
            skLineSegment(sketch, "E85.4", {"start": v(-74.25, -64.25) * mm, "end": v(-74.25, 64.25) * mm});
            skCircle(sketch, "E85.5", {"center": v(-60, 60) * mm, "radius": 4 * mm});
            skCircle(sketch, "E85.6", {"center": v(60, 60) * mm, "radius": 4 * mm});
            skArc(sketch, "E85.7", {"start": v(54.26, 47.88) * mm, "mid": v(0, 60) * mm, "end": v(-54.26, 47.88) * mm});
            skLineSegment(sketch, "E85.8", {"start": v(60, 38.83) * mm, "end": v(60, -38.83) * mm});
            skArc(sketch, "E85.9", {"start": v(60, 38.83) * mm, "mid": v(58.44, 44.2) * mm, "end": v(54.26, 47.88) * mm});
            skArc(sketch, "E85.10", {"start": v(-54.26, 47.88) * mm, "mid": v(-58.44, 44.2) * mm, "end": v(-60, 38.83) * mm});
            skLineSegment(sketch, "E85.11", {"start": v(-60, 38.83) * mm, "end": v(-60, -38.83) * mm});
            skArc(sketch, "E85.12", {"start": v(54.26, -47.88) * mm, "mid": v(58.44, -44.2) * mm, "end": v(60, -38.83) * mm});
            skArc(sketch, "E85.13", {"start": v(-54.26, -47.88) * mm, "mid": v(0, -60) * mm, "end": v(54.26, -47.88) * mm});
            skArc(sketch, "E85.14", {"start": v(-60, -38.83) * mm, "mid": v(-58.44, -44.2) * mm, "end": v(-54.26, -47.88) * mm});
            skArc(sketch, "E85.15", {"start": v(-74.25, -64.25) * mm, "mid": v(-71.32, -71.32) * mm, "end": v(-64.25, -74.25) * mm});
            skLineSegment(sketch, "E85.16", {"start": v(-64.25, -74.25) * mm, "end": v(64.25, -74.25) * mm});
            skCircle(sketch, "E85.17", {"center": v(-60, -60) * mm, "radius": 4 * mm});
            skCircle(sketch, "E85.18", {"center": v(60, -60) * mm, "radius": 4 * mm});
            skArc(sketch, "E85.19", {"start": v(64.25, -74.25) * mm, "mid": v(71.32, -71.32) * mm, "end": v(74.25, -64.25) * mm});
            skLineSegment(sketch, "E86", {"start": v(15, 92.25) * mm, "end": v(33, 74.25) * mm});
            skLineSegment(sketch, "E87", {"start": v(-15, 92.25) * mm, "end": v(-33, 74.25) * mm});
            skLineSegment(sketch, "E88", {"start": v(-74.25, 0) * mm, "end": v(74.25, 0) * mm, "construction": true});
            skLineSegment(sketch, "E89.MirrorCS", {"start": v(15, -92.25) * mm, "end": v(33, -74.25) * mm});
            skLineSegment(sketch, "E90.MirrorCS", {"start": v(15, -104.25) * mm, "end": v(15, -92.25) * mm});
            skArc(sketch, "E91.MirrorCS", {"start": v(-15, -104.25) * mm, "mid": v(0, -119.25) * mm, "end": v(15, -104.25) * mm});
            skLineSegment(sketch, "E92.MirrorCS", {"start": v(-15, -92.25) * mm, "end": v(-15, -104.25) * mm});
            skLineSegment(sketch, "E93.MirrorCS", {"start": v(-15, -92.25) * mm, "end": v(-33, -74.25) * mm});
            skCircle(sketch, "E94.MirrorC", {"center": v(0, -104.25) * mm, "radius": 6 * mm});
            skSolve(sketch);
        }
        {
            var Q0;
            Q0=makeQuery(id+"F16.imprint","IMPRINT",FACE,{"disambiguationData":[TD([[makeQuery(id+"F16.imprint","IMPRINT",EDGE,{"derivedFrom":sQuery(id+"F16.wireOp",EDGE,"E79")}),-1.0]])]});
            var Q1;
            {var subQ7=sQuery(id+"F16.wireOp",EDGE,"E85.1");Q1=makeQuery(id+"F16.imprint","IMPRINT",FACE,{"disambiguationData":[TD([[makeQuery(id+"F16.imprint","IMPRINT",EDGE,{"derivedFrom":subQ7}),1.0]])]});}
            var Q2;
            {var subQ0=sQuery(id+"F16.wireOp",EDGE,"E89.MirrorCS");Q2=makeQuery(id+"F16.imprint","IMPRINT",FACE,{"disambiguationData":[TD([[makeQuery(id+"F16.imprint","IMPRINT",EDGE,{"derivedFrom":subQ0}),1.0]])]});}
            var Q3;
            Q3=makeQuery(id+"F2.opExtrude","CAP_FACE",FACE,{"disambiguationData":[OSD([sQuery(id+"F0.wireOp",EDGE,"E12"),sQuery(id+"F0.wireOp",EDGE,"E13"),sQuery(id+"F0.wireOp",EDGE,"E14"),sQuery(id+"F0.wireOp",EDGE,"E15"),sQuery(id+"F0.wireOp",EDGE,"E17.filletArc"),sQuery(id+"F0.wireOp",EDGE,"E18.filletArc"),sQuery(id+"F0.wireOp",EDGE,"E19.filletArc"),sQuery(id+"F0.wireOp",EDGE,"E20.filletArc"),sQuery(id+"F0.wireOp",EDGE,"E25.0"),sQuery(id+"F0.wireOp",EDGE,"E25.1"),sQuery(id+"F0.wireOp",EDGE,"E25.2"),sQuery(id+"F0.wireOp",EDGE,"E25.3"),sQuery(id+"F0.wireOp",EDGE,"E25.4"),sQuery(id+"F0.wireOp",EDGE,"E25.5"),sQuery(id+"F0.wireOp",EDGE,"E25.6"),sQuery(id+"F0.wireOp",EDGE,"E25.7")])],"isStart":false});
            extrude(context, id + "F17", {"entities" : qUnion([Q0, Q1, Q2]), "endBound" : BoundingType.UP_TO_SURFACE, "depth" : 25 * mm, "endBoundEntityFace" : qUnion([Q3]), "offsetDistance" : 25 * mm});
        }
    });
